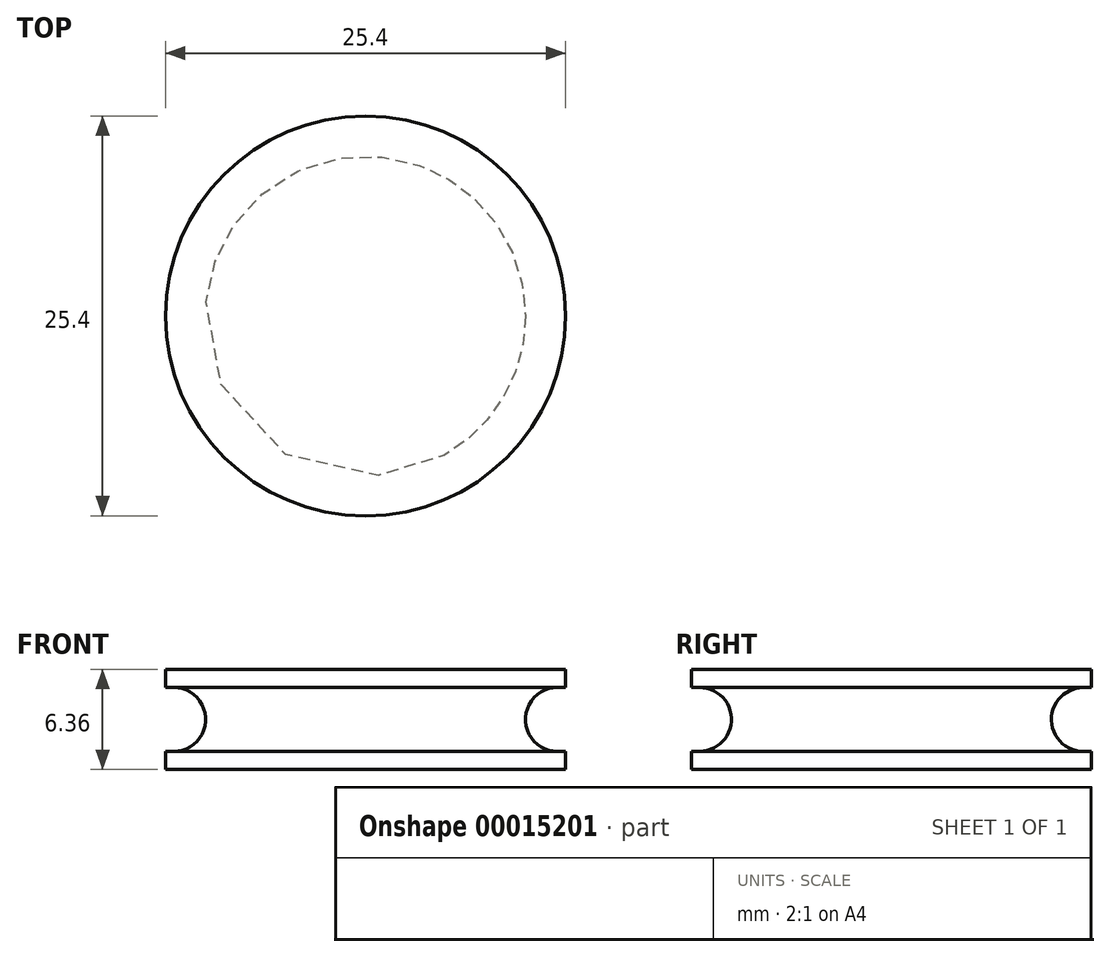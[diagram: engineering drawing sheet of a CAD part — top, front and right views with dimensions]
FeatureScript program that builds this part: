
annotation { "Feature Type Name" : "Feature", "Feature Type Description" : "" }
export const myFeature = defineFeature(function(context is Context, id is Id, definition is map)
    precondition{}
    {
        {
            var Q0;
            Q0=qCreatedBy(makeId("Top.planeOp"),FACE);
            var sketch = newSketch(context, id + "F0", { "sketchPlane" : qUnion([Q0])});
            skCircle(sketch, "E0", {"center": v(0, 0) * mm, "radius": 12.7 * mm});
            skSolve(sketch);
        }
        {
            var Q0;
            Q0 = qSketchRegion(id + "F0", true);
            extrude(context, id + "F1", {"entities" : qUnion([Q0]), "endBound" : BoundingType.SYMMETRIC, "depth" : 6.35 * mm});
        }
        {
            var Q0;
            Q0=qCreatedBy(makeId("Front.planeOp"),FACE);
            var sketch = newSketch(context, id + "F2", { "sketchPlane" : qUnion([Q0])});
            skLineSegment(sketch, "E1.bottom", {"start": v(-76.84, 2.03) * mm, "end": v(-12.2, 2.03) * mm});
            skLineSegment(sketch, "E1.top", {"start": v(-76.84, -2.03) * mm, "end": v(-12.2, -2.03) * mm});
            skLineSegment(sketch, "E1.left", {"start": v(-76.84, 2.03) * mm, "end": v(-76.84, -2.03) * mm});
            skArc(sketch, "E2", {"start": v(-12.2, -2.03) * mm, "mid": v(-10.16, 0) * mm, "end": v(-12.2, 2.03) * mm});
            skSolve(sketch);
        }
        {
            var Q0;
            Q0 = qSketchRegion(id + "F2", true);
            var Q1;
            Q1=makeQuery(id+"F1.opExtrude","CAP_EDGE",EDGE,{"disambiguationData":[OSD([sQuery(id+"F0.wireOp",EDGE,"E0")])],"isStart":false});
            revolve(context, id + "F3", {"operationType" : NewBodyOperationType.REMOVE, "entities" : qUnion([Q0]), "axis" : qUnion([Q1]), "revolveType" : RevolveType.FULL, "oppositeDirection" : true});
        }
    });
